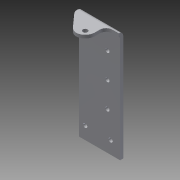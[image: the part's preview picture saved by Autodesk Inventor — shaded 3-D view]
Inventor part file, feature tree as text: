
AUTODESK INVENTOR PART (.ipt)
format: ipt  version: 2014 (Build 180170000, 170)  size: 205,824 bytes
history: native  units: in
note: dims shown in document units (in); Inventor stores cm internally (conversion verified against a paired STEP export)
features: other x5, sheet_metal_op x4, sketch x2, fillet x1
ambient origin geometry x8: Origin, YZ Plane, XZ Plane, XY Plane, X Axis, Y Axis, Z Axis, Center Point
bodies: Solid1 (feature_tree)
feature tree (12):
  sheet_metal_op  "Face1"
  sheet_metal_op  "Flange1"
  fillet  "Fillet3"  Radius=1.625in
  sketch  "Sketch1"  dims[d1=4.1875in]
  other  "Plate1"
  sketch  "Sketch2"  dims[d2=0.163in d3=0.25in d4=0.7874in d6=1.0in d7=0.3937in d9=1.0in d11=0.125in d12=0.125in d13=0.0625in d14=0.25in d15=0.125in d16=1.0in d17=90.0deg d18=0.05in d19=0.5in d20=0.125in d21=0.125in d22=0.5in d28=0.187in d29=0.25in d30=0.75in d31=0.125in d32=0.0in d36=0.5in d37=1.5in d38=1.1811in d40=1.0in d41=0.3937in d43=1.0in d45=0.125in d46=0.25in d47=0.25in d48=0.375in d49=0.25in]
  other  "Plate2"
  sheet_metal_op  "Bend1"
  sheet_metal_op  "Corner1"
  other  "Cut2"
  other  "Definition1"
  other  "Cut1"
